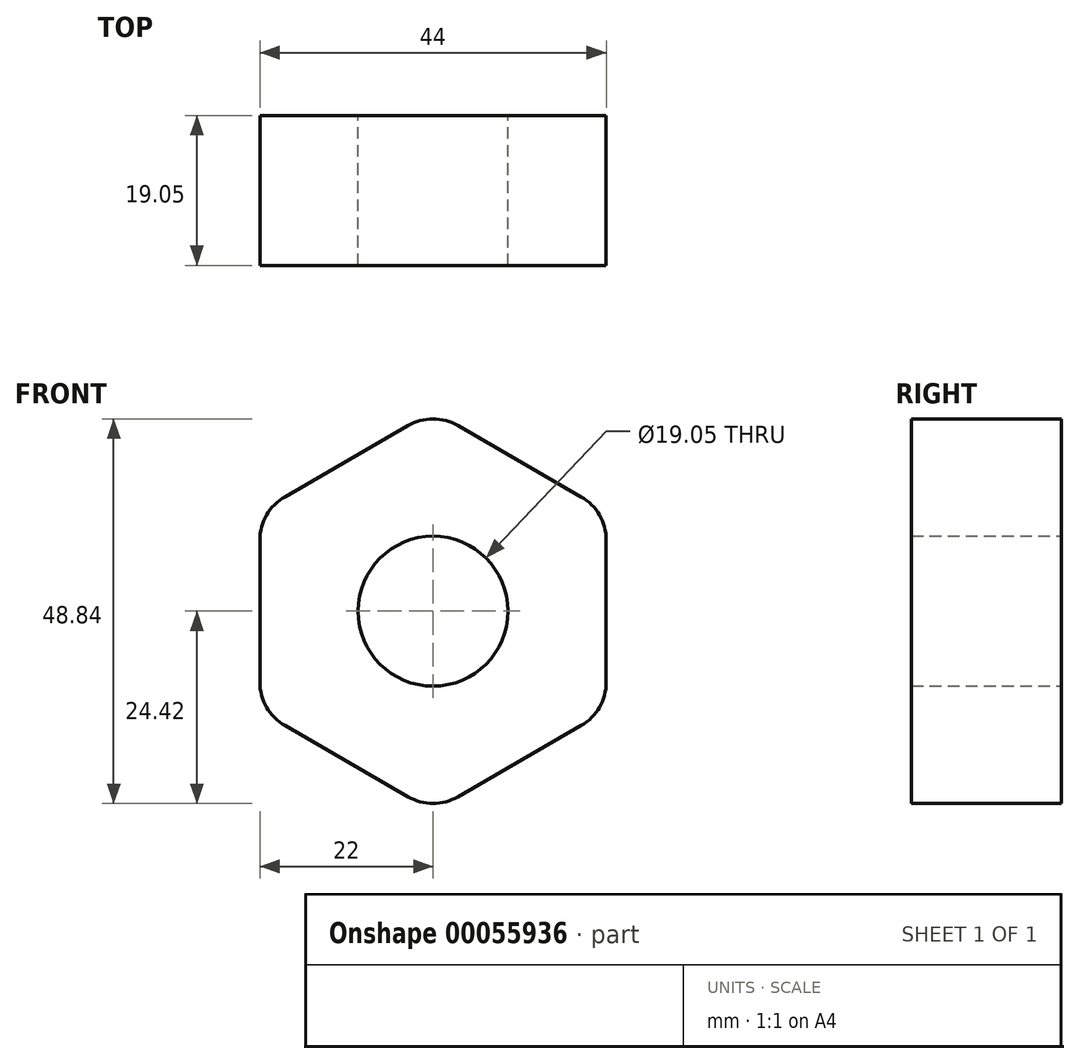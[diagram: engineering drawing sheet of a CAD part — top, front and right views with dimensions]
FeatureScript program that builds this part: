
annotation { "Feature Type Name" : "Feature", "Feature Type Description" : "" }
export const myFeature = defineFeature(function(context is Context, id is Id, definition is map)
    precondition{}
    {
        {
            var Q0;
            Q0=qCreatedBy(makeId("Front.planeOp"),FACE);
            var sketch = newSketch(context, id + "F0", { "sketchPlane" : qUnion([Q0])});
            skLineSegment(sketch, "E0", {"start": v(-18.82, 14.53) * mm, "end": v(-3.17, 23.57) * mm});
            skLineSegment(sketch, "E1", {"start": v(3.18, 23.57) * mm, "end": v(18.82, 14.53) * mm});
            skLineSegment(sketch, "E2", {"start": v(22, 9.03) * mm, "end": v(22, -9.03) * mm});
            skLineSegment(sketch, "E3", {"start": v(18.82, -14.53) * mm, "end": v(3.17, -23.57) * mm});
            skLineSegment(sketch, "E4", {"start": v(-3.18, -23.57) * mm, "end": v(-18.82, -14.53) * mm});
            skLineSegment(sketch, "E5", {"start": v(-22, -9.03) * mm, "end": v(-22, 9.03) * mm});
            skLineSegment(sketch, "E6", {"start": v(0, -25.4) * mm, "end": v(0, 0) * mm, "construction": true});
            skLineSegment(sketch, "E7", {"start": v(0, 0) * mm, "end": v(22, 12.7) * mm, "construction": true});
            skLineSegment(sketch, "E8", {"start": v(22, -12.7) * mm, "end": v(0, 0) * mm, "construction": true});
            skLineSegment(sketch, "E9", {"start": v(-22, 12.7) * mm, "end": v(0, 0) * mm, "construction": true});
            skLineSegment(sketch, "E10", {"start": v(-22, -12.7) * mm, "end": v(0, 0) * mm, "construction": true});
            skLineSegment(sketch, "E11", {"start": v(0, 25.4) * mm, "end": v(0, 0) * mm, "construction": true});
            skPoint(sketch, "E12.visualSharp", {"position": v(0, 25.4) * mm});
            skArc(sketch, "E12.filletArc", {"start": v(3.18, 23.57) * mm, "mid": v(0, 24.42) * mm, "end": v(-3.17, 23.57) * mm});
            skPoint(sketch, "E13.visualSharp", {"position": v(22, 12.7) * mm});
            skArc(sketch, "E13.filletArc", {"start": v(22, 9.03) * mm, "mid": v(21.15, 12.2) * mm, "end": v(18.82, 14.53) * mm});
            skPoint(sketch, "E14.visualSharp", {"position": v(22, -12.7) * mm});
            skArc(sketch, "E14.filletArc", {"start": v(18.82, -14.53) * mm, "mid": v(21.15, -12.2) * mm, "end": v(22, -9.03) * mm});
            skPoint(sketch, "E15.visualSharp", {"position": v(0, -25.4) * mm});
            skArc(sketch, "E15.filletArc", {"start": v(-3.18, -23.57) * mm, "mid": v(0, -24.42) * mm, "end": v(3.17, -23.57) * mm});
            skPoint(sketch, "E16.visualSharp", {"position": v(-22, -12.7) * mm});
            skArc(sketch, "E16.filletArc", {"start": v(-22, -9.03) * mm, "mid": v(-21.15, -12.2) * mm, "end": v(-18.82, -14.53) * mm});
            skPoint(sketch, "E17.visualSharp", {"position": v(-22, 12.7) * mm});
            skArc(sketch, "E17.filletArc", {"start": v(-18.82, 14.53) * mm, "mid": v(-21.15, 12.2) * mm, "end": v(-22, 9.03) * mm});
            skCircle(sketch, "E18", {"center": v(0, 0) * mm, "radius": 9.53 * mm});
            skSolve(sketch);
        }
        {
            var Q0;
            Q0=makeQuery(id+"F0.imprint","IMPRINT",FACE,{"disambiguationData":[TD([[makeQuery(id+"F0.imprint","IMPRINT",EDGE,{"derivedFrom":sQuery(id+"F0.wireOp",EDGE,"E0")}),-1.0]])]});
            extrude(context, id + "F1", {"entities" : qUnion([Q0]), "depth" : 19.05 * mm});
        }
    });
